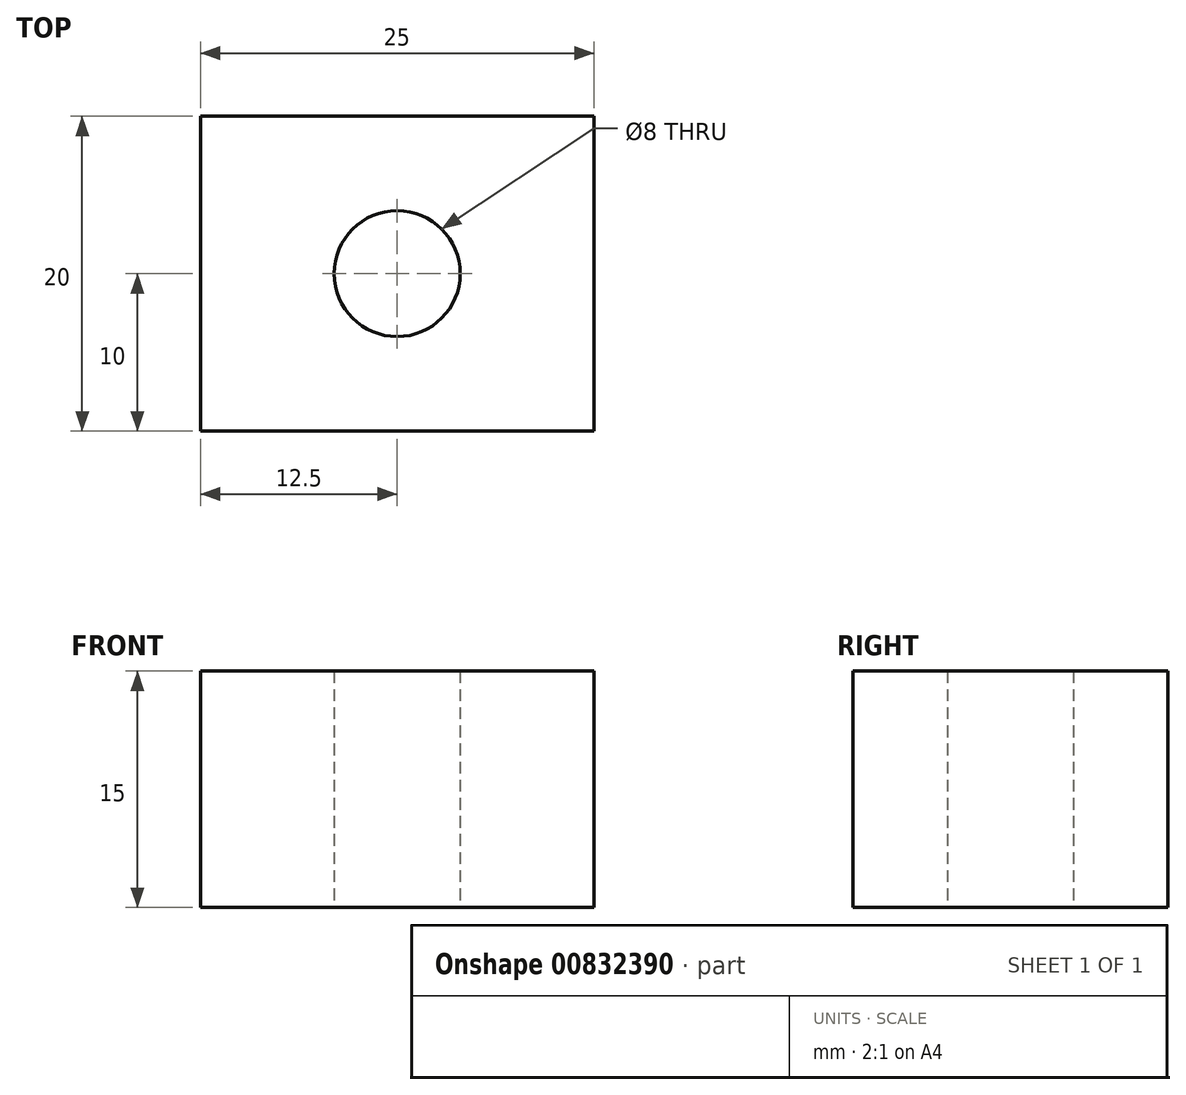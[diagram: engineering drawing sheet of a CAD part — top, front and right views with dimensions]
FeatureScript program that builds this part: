
annotation { "Feature Type Name" : "Feature", "Feature Type Description" : "" }
export const myFeature = defineFeature(function(context is Context, id is Id, definition is map)
    precondition{}
    {
        {
            var Q0;
            Q0=qCreatedBy(makeId("Top.planeOp"),FACE);
            var sketch = newSketch(context, id + "F0", { "sketchPlane" : qUnion([Q0])});
            skLineSegment(sketch, "E0.bottom", {"start": v(0, 0) * mm, "end": v(25, 0) * mm});
            skLineSegment(sketch, "E0.top", {"start": v(0, 20) * mm, "end": v(25, 20) * mm});
            skLineSegment(sketch, "E0.left", {"start": v(0, 0) * mm, "end": v(0, 20) * mm});
            skLineSegment(sketch, "E0.right", {"start": v(25, 0) * mm, "end": v(25, 20) * mm});
            skCircle(sketch, "E1", {"center": v(12.5, 10) * mm, "radius": 4 * mm});
            skLineSegment(sketch, "E2", {"start": v(0, 10) * mm, "end": v(12.5, 10) * mm, "construction": true});
            skLineSegment(sketch, "E3", {"start": v(12.5, 20) * mm, "end": v(12.5, 10) * mm, "construction": true});
            skSolve(sketch);
        }
        {
            var Q0;
            Q0=makeQuery(id+"F0.imprint","IMPRINT",FACE,{"disambiguationData":[TD([[makeQuery(id+"F0.imprint","IMPRINT",EDGE,{"derivedFrom":sQuery(id+"F0.wireOp",EDGE,"E0.bottom")}),1.0]])]});
            extrude(context, id + "F1", {"entities" : qUnion([Q0]), "depth" : 15 * mm, "offsetDistance" : 25.4 * mm});
        }
    });
